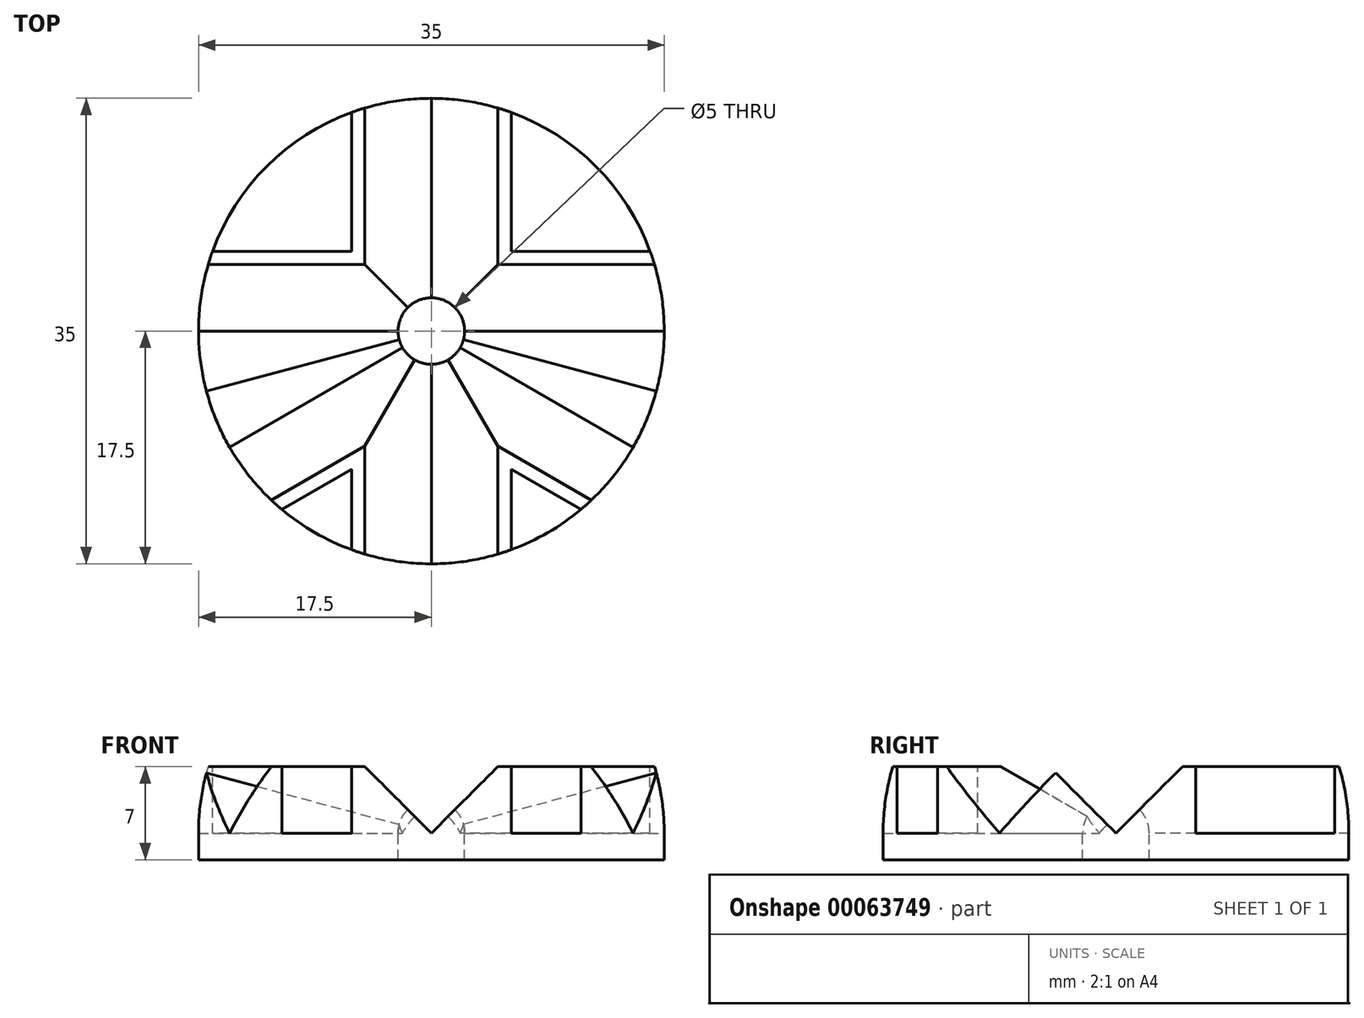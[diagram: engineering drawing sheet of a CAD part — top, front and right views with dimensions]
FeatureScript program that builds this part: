
annotation { "Feature Type Name" : "Feature", "Feature Type Description" : "" }
export const myFeature = defineFeature(function(context is Context, id is Id, definition is map)
    precondition{}
    {
        {
            var Q0;
            Q0=qCreatedBy(makeId("Top.planeOp"),FACE);
            var sketch = newSketch(context, id + "F0", { "sketchPlane" : qUnion([Q0])});
            skCircle(sketch, "E0", {"center": v(0, 0) * mm, "radius": 17.5 * mm});
            skLineSegment(sketch, "E1", {"start": v(0, 0) * mm, "end": v(0, 17.5) * mm, "construction": true});
            skLineSegment(sketch, "E2", {"start": v(0, 0) * mm, "end": v(17.5, 0) * mm, "construction": true});
            skLineSegment(sketch, "E3", {"start": v(0, 0) * mm, "end": v(0, -17.5) * mm, "construction": true});
            skLineSegment(sketch, "E4", {"start": v(0, 0) * mm, "end": v(-17.5, 0) * mm, "construction": true});
            skLineSegment(sketch, "E5", {"start": v(0, 0) * mm, "end": v(15.16, -8.75) * mm, "construction": true});
            skLineSegment(sketch, "E6", {"start": v(0, 0) * mm, "end": v(-15.16, -8.75) * mm, "construction": true});
            skSolve(sketch);
        }
        {
            var Q0;
            Q0 = qSketchRegion(id + "F0", true);
            extrude(context, id + "F1", {"entities" : qUnion([Q0]), "depth" : 10 * mm});
        }
        {
            var Q0;
            Q0=qCreatedBy(makeId("Front.planeOp"),FACE);
            var sketch = newSketch(context, id + "F2", { "sketchPlane" : qUnion([Q0])});
            skLineSegment(sketch, "E7", {"start": v(0, 0) * mm, "end": v(10, 10) * mm});
            skLineSegment(sketch, "E8", {"start": v(0, 0) * mm, "end": v(6.4, 0) * mm, "construction": true});
            skLineSegment(sketch, "E9", {"start": v(0, 0) * mm, "end": v(-10, 10) * mm});
            skLineSegment(sketch, "E10", {"start": v(-10, 10) * mm, "end": v(10, 10) * mm});
            skSolve(sketch);
        }
        {
            var Q0;
            Q0=qCreatedBy(makeId("Right.planeOp"),FACE);
            var sketch = newSketch(context, id + "F3", { "sketchPlane" : qUnion([Q0])});
            skLineSegment(sketch, "E11", {"start": v(-10, 10) * mm, "end": v(0, 0) * mm});
            skLineSegment(sketch, "E12", {"start": v(0, 0) * mm, "end": v(10, 10) * mm});
            skLineSegment(sketch, "E13", {"start": v(0, 0) * mm, "end": v(9.24, 0) * mm, "construction": true});
            skLineSegment(sketch, "E14", {"start": v(-10, 10) * mm, "end": v(10, 10) * mm});
            skSolve(sketch);
        }
        {
            var Q0;
            Q0 = qSketchRegion(id + "F2", true);
            extrude(context, id + "F4", {"entities" : qUnion([Q0]), "operationType" : NewBodyOperationType.REMOVE, "endBound" : BoundingType.THROUGH_ALL, "oppositeDirection" : true, "depth" : 25 * mm, "hasSecondDirection" : true, "secondDirectionBound" : SecondDirectionBoundingType.THROUGH_ALL, "secondDirectionOppositeDirection" : false, "secondDirectionDepth" : 25 * mm});
        }
        {
            var Q0;
            Q0 = qSketchRegion(id + "F3", true);
            extrude(context, id + "F5", {"entities" : qUnion([Q0]), "operationType" : NewBodyOperationType.REMOVE, "endBound" : BoundingType.THROUGH_ALL, "oppositeDirection" : true, "depth" : 25 * mm, "hasSecondDirection" : true, "secondDirectionBound" : SecondDirectionBoundingType.THROUGH_ALL, "secondDirectionOppositeDirection" : false, "secondDirectionDepth" : 25 * mm});
        }
        {
            var Q0;
            Q0=sQuery(id+"F0.wireOp",EDGE,"E5");
            var Q1;
            Q1=sQuery(id+"F0.wireOp",VERTEX,"E6.start");
            cPlane(context, id + "F6", {"entities" : qUnion([Q0, Q1]), "cplaneType" : CPlaneType.CURVE_POINT, "offset" : 150 * mm, "width" : 150 * mm, "height" : 150 * mm});
        }
        {
            var Q0;
            Q0=qCreatedBy(id+"F6.planeOp",FACE);
            var sketch = newSketch(context, id + "F7", { "sketchPlane" : qUnion([Q0])});
            skLineSegment(sketch, "E15", {"start": v(-10.01, 10.01) * mm, "end": v(0, 0) * mm});
            skLineSegment(sketch, "E16", {"start": v(0, 0) * mm, "end": v(10, 10) * mm});
            skLineSegment(sketch, "E17", {"start": v(10, 10) * mm, "end": v(-10.01, 10.01) * mm});
            skLineSegment(sketch, "E18", {"start": v(0, 0) * mm, "end": v(10.56, 0) * mm, "construction": true});
            skSolve(sketch);
        }
        {
            var Q0;
            Q0 = qSketchRegion(id + "F7", true);
            extrude(context, id + "F8", {"entities" : qUnion([Q0]), "operationType" : NewBodyOperationType.REMOVE, "endBound" : BoundingType.THROUGH_ALL, "depth" : 25 * mm});
        }
        {
            var Q0;
            Q0=sQuery(id+"F0.wireOp",EDGE,"E6");
            var Q1;
            Q1=sQuery(id+"F0.wireOp",VERTEX,"E0.center");
            cPlane(context, id + "F9", {"entities" : qUnion([Q0, Q1]), "cplaneType" : CPlaneType.CURVE_POINT, "offset" : 150 * mm, "width" : 150 * mm, "height" : 150 * mm});
        }
        {
            var Q0;
            Q0=qCreatedBy(id+"F9.planeOp",FACE);
            var sketch = newSketch(context, id + "F10", { "sketchPlane" : qUnion([Q0])});
            skLineSegment(sketch, "E19", {"start": v(10, 10) * mm, "end": v(0, 0) * mm});
            skLineSegment(sketch, "E20", {"start": v(0, 0) * mm, "end": v(-10, 10) * mm});
            skLineSegment(sketch, "E21", {"start": v(-10, 10) * mm, "end": v(10, 10) * mm});
            skLineSegment(sketch, "E22", {"start": v(0, 0) * mm, "end": v(16.2, 0) * mm, "construction": true});
            skSolve(sketch);
        }
        {
            var Q0;
            Q0 = qSketchRegion(id + "F10", true);
            extrude(context, id + "F11", {"entities" : qUnion([Q0]), "operationType" : NewBodyOperationType.REMOVE, "endBound" : BoundingType.THROUGH_ALL, "depth" : 25 * mm});
        }
        {
            var Q0;
            Q0 = qSketchRegion(id + "F0", true);
            extrude(context, id + "F12", {"entities" : qUnion([Q0]), "operationType" : NewBodyOperationType.ADD, "oppositeDirection" : true, "depth" : 2 * mm});
        }
        {
            var Q0;
            Q0=qCreatedBy(makeId("Top.planeOp"),FACE);
            var sketch = newSketch(context, id + "F13", { "sketchPlane" : qUnion([Q0])});
            skCircle(sketch, "E23", {"center": v(0, 0) * mm, "radius": 2.5 * mm});
            skSolve(sketch);
        }
        {
            var Q0;
            Q0 = qSketchRegion(id + "F13", true);
            extrude(context, id + "F14", {"entities" : qUnion([Q0]), "operationType" : NewBodyOperationType.REMOVE, "endBound" : BoundingType.THROUGH_ALL, "oppositeDirection" : true, "depth" : 25 * mm, "hasSecondDirection" : true, "secondDirectionBound" : SecondDirectionBoundingType.THROUGH_ALL, "secondDirectionOppositeDirection" : false, "secondDirectionDepth" : 25 * mm});
        }
        {
            var Q0;
            Q0=qCreatedBy(makeId("Top.planeOp"),FACE);
            cPlane(context, id + "F15", {"entities" : qUnion([Q0]), "cplaneType" : CPlaneType.OFFSET, "offset" : 5 * mm, "width" : 150 * mm, "height" : 150 * mm});
        }
        {
            var Q0;
            Q0=qCreatedBy(id+"F15.planeOp",FACE);
            var sketch = newSketch(context, id + "F16", { "sketchPlane" : qUnion([Q0])});
            skCircle(sketch, "E24", {"center": v(0, 0) * mm, "radius": 17.5 * mm});
            skSolve(sketch);
        }
        {
            var Q0;
            Q0 = qSketchRegion(id + "F16", true);
            extrude(context, id + "F17", {"entities" : qUnion([Q0]), "operationType" : NewBodyOperationType.REMOVE, "endBound" : BoundingType.THROUGH_ALL, "depth" : 25 * mm});
        }
        {
            var Q0;
            {var subQ2=makeQuery(id+"F4.boolean.opBoolean","COPY",FACE,{"derivedFrom":makeQuery(id+"F4.opExtrude","SWEPT_FACE",FACE,{"disambiguationData":[OSD([sQuery(id+"F2.wireOp",EDGE,"E9")])]})});Q0=makeQuery(id+"F17.boolean.opBoolean","COPY",FACE,{"disambiguationData":[TD([makeQuery(id+"F5.boolean.opBoolean","COPY",FACE,{"disambiguationData":[TD([subQ2])],"derivedFrom":makeQuery(id+"F5.opExtrude","SWEPT_FACE",FACE,{"disambiguationData":[OSD([sQuery(id+"F3.wireOp",EDGE,"E12")])]})})])],"derivedFrom":makeQuery(id+"F17.opExtrude","CAP_FACE",FACE,{"disambiguationData":[OSD([sQuery(id+"F16.wireOp",EDGE,"E24")])],"isStart":true})});}
            var sketch = newSketch(context, id + "F18", { "sketchPlane" : qUnion([Q0])});
            skLineSegment(sketch, "E25.0", {"start": v(-16.44, 6) * mm, "end": v(-6, 6) * mm});
            skLineSegment(sketch, "E25.1", {"start": v(-6, 16.44) * mm, "end": v(-6, 6) * mm});
            skArc(sketch, "E26.0", {"start": v(-6, 16.44) * mm, "mid": v(-12.37, 12.37) * mm, "end": v(-16.44, 6) * mm});
            skLineSegment(sketch, "E27.MirrorCS", {"start": v(6, 16.44) * mm, "end": v(6, 6) * mm});
            skLineSegment(sketch, "E28.MirrorCS", {"start": v(16.44, 6) * mm, "end": v(6, 6) * mm});
            skArc(sketch, "E29.MirrorCS", {"start": v(6, 16.44) * mm, "mid": v(12.37, 12.37) * mm, "end": v(16.44, 6) * mm});
            skSolve(sketch);
        }
        {
            var Q0;
            Q0 = qSketchRegion(id + "F18", true);
            extrude(context, id + "F19", {"entities" : qUnion([Q0]), "operationType" : NewBodyOperationType.REMOVE, "oppositeDirection" : true, "depth" : 5 * mm});
        }
        {
            var Q0;
            Q0=makeQuery(id+"F17.boolean.opBoolean","COPY",FACE,{"disambiguationData":[TD([makeQuery(id+"F8.boolean.opBoolean","COPY",FACE,{"derivedFrom":makeQuery(id+"F8.opExtrude","SWEPT_FACE",FACE,{"disambiguationData":[OSD([sQuery(id+"F7.wireOp",EDGE,"E15")])]})})])],"derivedFrom":makeQuery(id+"F17.opExtrude","CAP_FACE",FACE,{"disambiguationData":[OSD([sQuery(id+"F16.wireOp",EDGE,"E24")])],"isStart":true})});
            var sketch = newSketch(context, id + "F20", { "sketchPlane" : qUnion([Q0])});
            skLineSegment(sketch, "E30.0", {"start": v(-6, -10.4) * mm, "end": v(-11.24, -13.42) * mm});
            skLineSegment(sketch, "E31.0", {"start": v(-6, -10.4) * mm, "end": v(-6, -16.44) * mm});
            skArc(sketch, "E32.0", {"start": v(-11.24, -13.42) * mm, "mid": v(-8.75, -15.16) * mm, "end": v(-6, -16.44) * mm});
            skArc(sketch, "E33.MirrorCS", {"start": v(11.24, -13.42) * mm, "mid": v(8.75, -15.16) * mm, "end": v(6, -16.44) * mm});
            skLineSegment(sketch, "E34.MirrorCS", {"start": v(6, -10.4) * mm, "end": v(11.24, -13.42) * mm});
            skLineSegment(sketch, "E35.MirrorCS", {"start": v(6, -10.4) * mm, "end": v(6, -16.44) * mm});
            skSolve(sketch);
        }
        {
            var Q0;
            Q0 = qSketchRegion(id + "F20", true);
            extrude(context, id + "F21", {"entities" : qUnion([Q0]), "operationType" : NewBodyOperationType.REMOVE, "oppositeDirection" : true, "depth" : 5 * mm});
        }
    });
